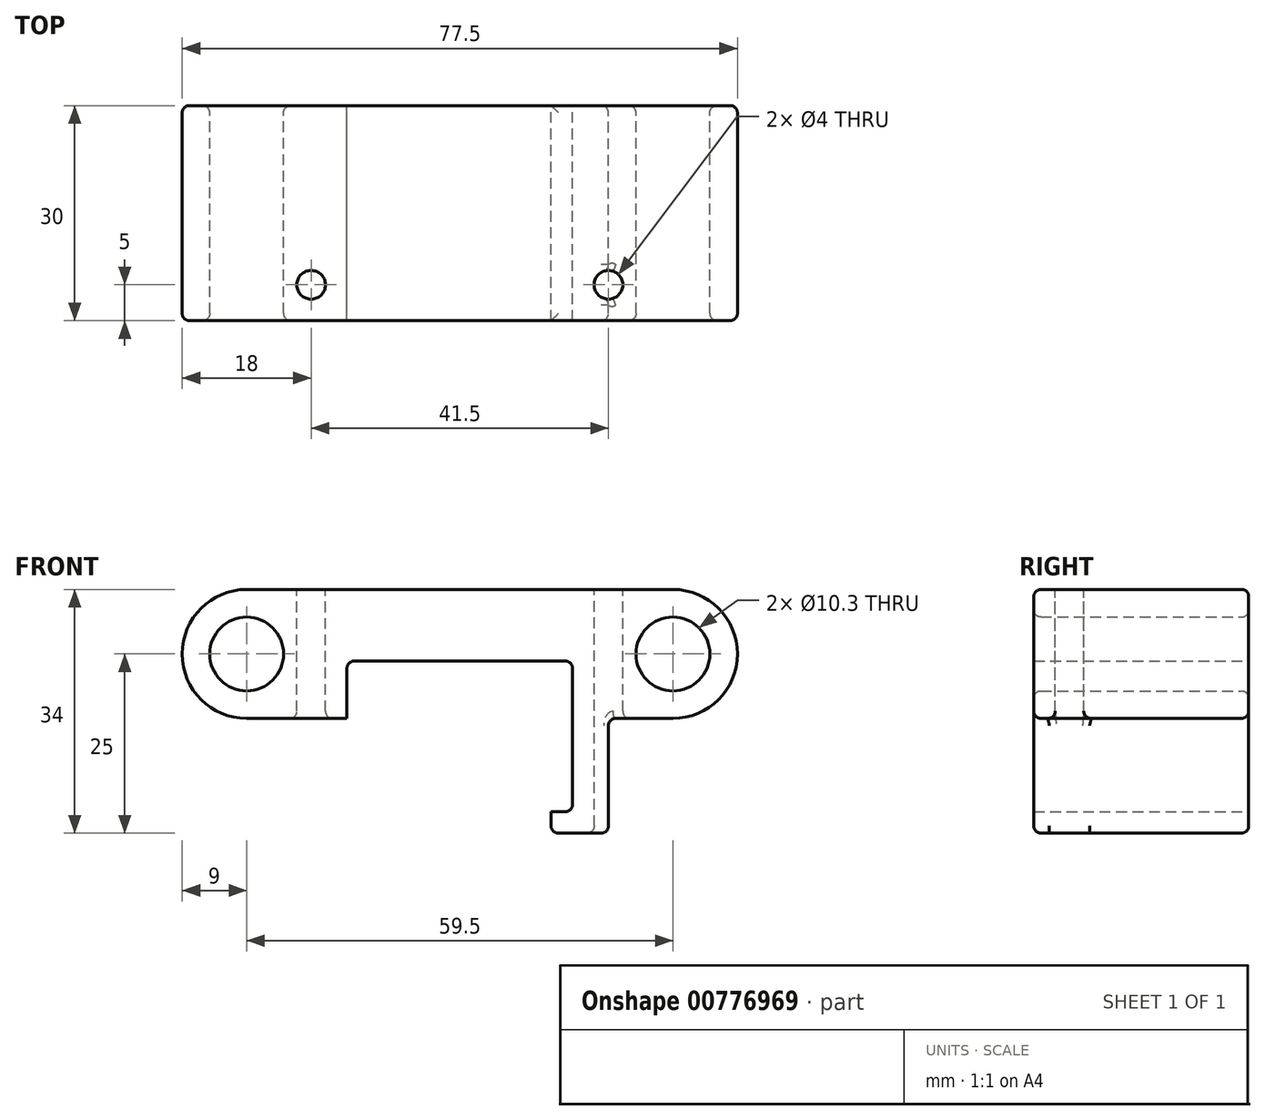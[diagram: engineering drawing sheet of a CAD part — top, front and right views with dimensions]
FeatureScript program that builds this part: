
annotation { "Feature Type Name" : "Feature", "Feature Type Description" : "" }
export const myFeature = defineFeature(function(context is Context, id is Id, definition is map)
    precondition{}
    {
        {
            var Q0;
            Q0=qCreatedBy(makeId("Front.planeOp"),FACE);
            var sketch = newSketch(context, id + "F0", { "sketchPlane" : qUnion([Q0])});
            skCircle(sketch, "E0", {"center": v(0, 0) * mm, "radius": 5.15 * mm});
            skCircle(sketch, "E1", {"center": v(59.5, 0) * mm, "radius": 5.15 * mm});
            skCircle(sketch, "E2", {"center": v(0, 0) * mm, "radius": 9 * mm});
            skCircle(sketch, "E3", {"center": v(59.5, 0) * mm, "radius": 9 * mm});
            skLineSegment(sketch, "E4", {"start": v(0, 9) * mm, "end": v(59.5, 9) * mm});
            skLineSegment(sketch, "E5", {"start": v(8.94, -1) * mm, "end": v(50.56, -1) * mm});
            skLineSegment(sketch, "E6", {"start": v(14, -1) * mm, "end": v(14, -9) * mm});
            skLineSegment(sketch, "E7", {"start": v(14, -9) * mm, "end": v(0, -9) * mm});
            skLineSegment(sketch, "E8", {"start": v(45.5, -1) * mm, "end": v(45.5, -22) * mm});
            skLineSegment(sketch, "E9", {"start": v(45.5, -22) * mm, "end": v(42.5, -22) * mm});
            skLineSegment(sketch, "E10", {"start": v(42.5, -22) * mm, "end": v(42.5, -25) * mm});
            skLineSegment(sketch, "E11", {"start": v(42.5, -25) * mm, "end": v(50.5, -25) * mm});
            skLineSegment(sketch, "E12", {"start": v(50.5, -25) * mm, "end": v(50.5, -9) * mm});
            skLineSegment(sketch, "E13", {"start": v(50.5, -9) * mm, "end": v(59.5, -9) * mm});
            skSolve(sketch);
        }
        {
            var Q0;
            Q0=qSketchRegion(id+"F0",true);
            extrude(context, id + "F1", {"entities" : qUnion([Q0]), "depth" : 30 * mm});
        }
        {
            var Q0;
            Q0=makeQuery(id+"F1.opExtrude","CAP_EDGE",EDGE,{"disambiguationData":[OSD([sQuery(id+"F0.wireOp",EDGE,"E2")])],"isStart":false});
            var Q1;
            Q1=makeQuery(id+"F1.opExtrude","CAP_EDGE",EDGE,{"disambiguationData":[OSD([sQuery(id+"F0.wireOp",EDGE,"E0")])],"isStart":false});
            var Q2;
            Q2=makeQuery(id+"F1.opExtrude","CAP_EDGE",EDGE,{"disambiguationData":[OSD([sQuery(id+"F0.wireOp",EDGE,"E1")])],"isStart":false});
            var Q3;
            Q3=makeQuery(id+"F1.opExtrude","CAP_EDGE",EDGE,{"disambiguationData":[OSD([sQuery(id+"F0.wireOp",EDGE,"E3")])],"isStart":true});
            var Q4;
            Q4=makeQuery(id+"F1.opExtrude","CAP_EDGE",EDGE,{"disambiguationData":[OSD([sQuery(id+"F0.wireOp",EDGE,"E1")])],"isStart":true});
            var Q5;
            Q5=makeQuery(id+"F1.opExtrude","CAP_EDGE",EDGE,{"disambiguationData":[OSD([sQuery(id+"F0.wireOp",EDGE,"E0")])],"isStart":true});
            fillet(context, id + "F2", {"entities" : qUnion([Q0, Q1, Q2, Q3, Q4, Q5]), "radius" : 1 * mm, "tangentPropagation" : true, "allowEdgeOverflow" : false});
        }
        {
            var Q0;
            Q0=makeQuery(id+"F1.opExtrude","SWEPT_EDGE",EDGE,{"disambiguationData":[OSD([sQuery(id+"F0.wireOp",EDGE,"E5"),sQuery(id+"F0.wireOp",EDGE,"E6")])]});
            var Q1;
            Q1=makeQuery(id+"F1.opExtrude","SWEPT_EDGE",EDGE,{"disambiguationData":[OSD([sQuery(id+"F0.wireOp",EDGE,"E5"),sQuery(id+"F0.wireOp",EDGE,"E8")])]});
            var Q2;
            Q2=makeQuery(id+"F1.opExtrude","SWEPT_EDGE",EDGE,{"disambiguationData":[OSD([sQuery(id+"F0.wireOp",EDGE,"E8"),sQuery(id+"F0.wireOp",EDGE,"E9")])]});
            var Q3;
            Q3=makeQuery(id+"F1.opExtrude","SWEPT_EDGE",EDGE,{"disambiguationData":[OSD([sQuery(id+"F0.wireOp",EDGE,"E12"),sQuery(id+"F0.wireOp",EDGE,"E13")])]});
            var Q4;
            Q4=makeQuery(id+"F1.opExtrude","SWEPT_EDGE",EDGE,{"disambiguationData":[OSD([sQuery(id+"F0.wireOp",EDGE,"E11"),sQuery(id+"F0.wireOp",EDGE,"E12")])]});
            var Q5;
            Q5=makeQuery(id+"F1.opExtrude","SWEPT_EDGE",EDGE,{"disambiguationData":[OSD([sQuery(id+"F0.wireOp",EDGE,"E10"),sQuery(id+"F0.wireOp",EDGE,"E11")])]});
            var Q6;
            Q6=makeQuery(id+"F1.opExtrude","CAP_EDGE",EDGE,{"disambiguationData":[OSD([sQuery(id+"F0.wireOp",EDGE,"E12")])],"isStart":false});
            var Q7;
            Q7=makeQuery(id+"F1.opExtrude","CAP_EDGE",EDGE,{"disambiguationData":[OSD([sQuery(id+"F0.wireOp",EDGE,"E11")])],"isStart":false});
            var Q8;
            Q8=makeQuery(id+"F1.opExtrude","CAP_EDGE",EDGE,{"disambiguationData":[OSD([sQuery(id+"F0.wireOp",EDGE,"E11")])],"isStart":true});
            var Q9;
            Q9=makeQuery(id+"F1.opExtrude","CAP_EDGE",EDGE,{"disambiguationData":[OSD([sQuery(id+"F0.wireOp",EDGE,"E12")])],"isStart":true});
            fillet(context, id + "F3", {"entities" : qUnion([Q0, Q1, Q2, Q3, Q4, Q5, Q6, Q7, Q8, Q9]), "radius" : 1 * mm, "tangentPropagation" : true, "allowEdgeOverflow" : false});
        }
        {
            var Q0;
            Q0=makeQuery(id+"F1.opExtrude","SWEPT_FACE",FACE,{"disambiguationData":[OSD([sQuery(id+"F0.wireOp",EDGE,"E4")])]});
            var sketch = newSketch(context, id + "F4", { "sketchPlane" : qUnion([Q0])});
            skCircle(sketch, "E14", {"center": v(9, -25) * mm, "radius": 2 * mm});
            skCircle(sketch, "E15", {"center": v(50.5, -25) * mm, "radius": 2 * mm});
            skSolve(sketch);
        }
        {
            var Q0;
            Q0=qSketchRegion(id+"F4",true);
            extrude(context, id + "F5", {"entities" : qUnion([Q0]), "operationType" : NewBodyOperationType.REMOVE, "endBound" : BoundingType.THROUGH_ALL, "oppositeDirection" : true, "depth" : 25 * mm});
        }
        {
            var Q0;
            Q0=makeQuery(id+"F5.boolean.opBoolean","COPY",EDGE,{"derivedFrom":makeQuery(id+"F5.opExtrude","CAP_EDGE",EDGE,{"disambiguationData":[OSD([sQuery(id+"F4.wireOp",EDGE,"E14")])],"isStart":true})});
            var Q1;
            Q1=makeQuery(id+"F5.boolean.opBoolean","COPY",EDGE,{"derivedFrom":makeQuery(id+"F5.opExtrude","CAP_EDGE",EDGE,{"disambiguationData":[OSD([sQuery(id+"F4.wireOp",EDGE,"E15")])],"isStart":true})});
            var Q2;
            Q2=makeQuery(id+"F5.boolean.opBoolean","INTERSECT",EDGE,{"derivedFrom":[makeQuery(id+"F1.opExtrude","SWEPT_FACE",FACE,{"disambiguationData":[OSD([sQuery(id+"F0.wireOp",EDGE,"E7")])]}),makeQuery(id+"F5.opExtrude","SWEPT_FACE",FACE,{"disambiguationData":[OSD([sQuery(id+"F4.wireOp",EDGE,"E14")])]})]});
            var Q3;
            Q3=makeQuery(id+"F5.boolean.opBoolean","INTERSECT",EDGE,{"derivedFrom":[makeQuery(id+"F1.opExtrude","SWEPT_FACE",FACE,{"disambiguationData":[OSD([sQuery(id+"F0.wireOp",EDGE,"E11")])]}),makeQuery(id+"F5.opExtrude","SWEPT_FACE",FACE,{"disambiguationData":[OSD([sQuery(id+"F4.wireOp",EDGE,"E15")])]})]});
            fillet(context, id + "F6", {"entities" : qUnion([Q0, Q1, Q2, Q3]), "radius" : 1 * mm, "tangentPropagation" : true, "allowEdgeOverflow" : false});
        }
    });
